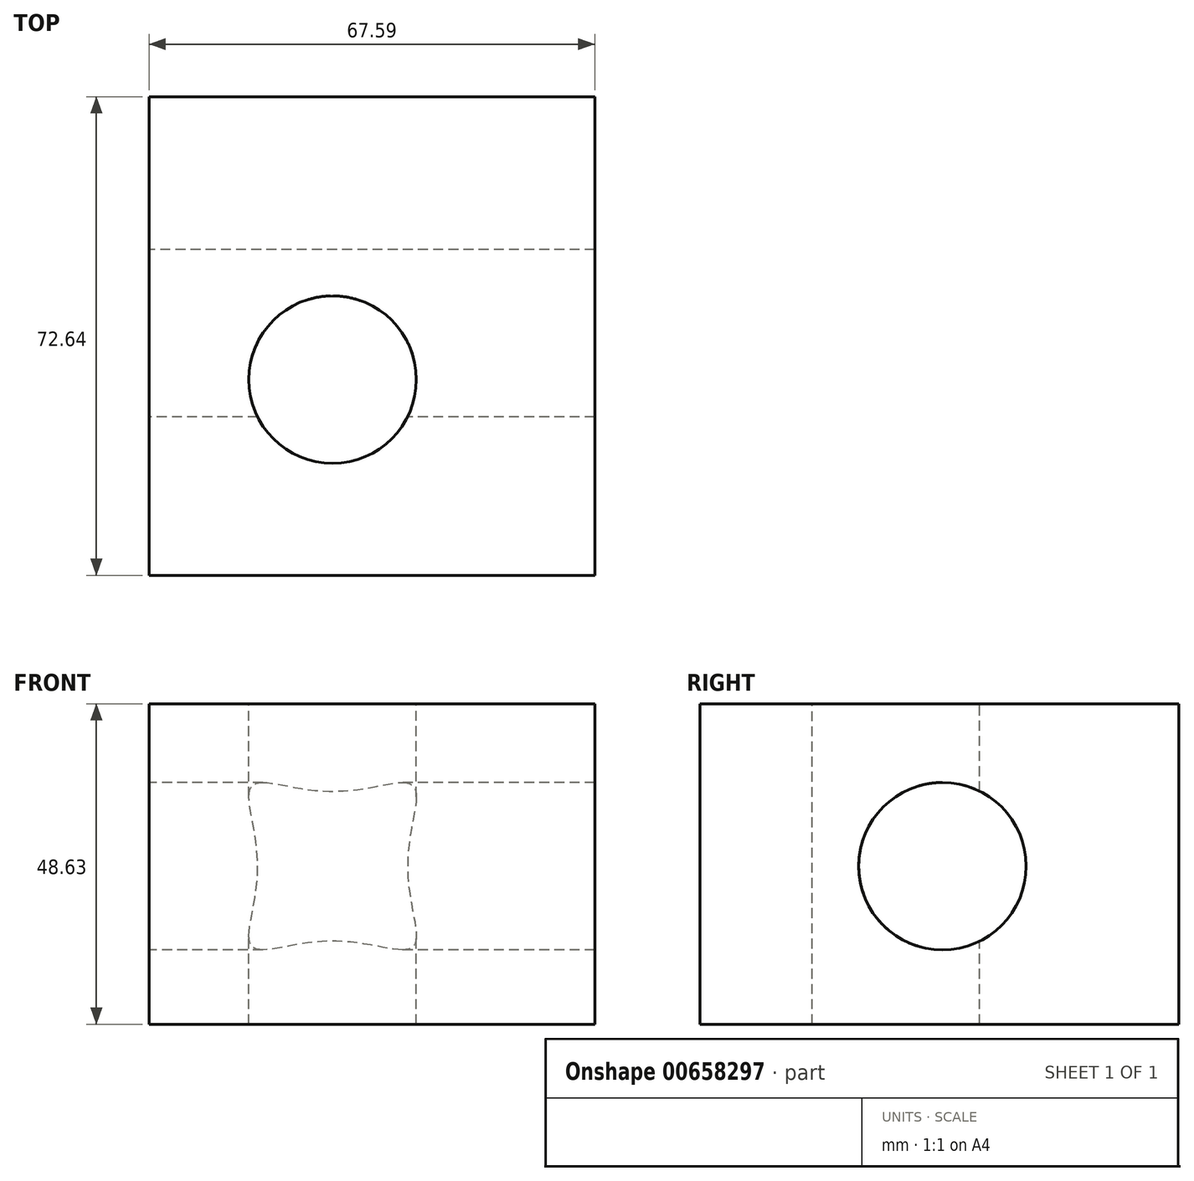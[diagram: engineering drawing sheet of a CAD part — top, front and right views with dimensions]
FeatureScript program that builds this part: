
annotation { "Feature Type Name" : "Feature", "Feature Type Description" : "" }
export const myFeature = defineFeature(function(context is Context, id is Id, definition is map)
    precondition{}
    {
        {
            var Q0;
            Q0=qCreatedBy(makeId("Front.planeOp"),FACE);
            var sketch = newSketch(context, id + "F0", { "sketchPlane" : qUnion([Q0])});
            skLineSegment(sketch, "E0.bottom", {"start": v(0, 0) * mm, "end": v(67.6, 0) * mm});
            skLineSegment(sketch, "E0.top", {"start": v(0, 48.63) * mm, "end": v(67.6, 48.63) * mm});
            skLineSegment(sketch, "E0.left", {"start": v(0, 0) * mm, "end": v(0, 48.63) * mm});
            skLineSegment(sketch, "E0.right", {"start": v(67.6, 0) * mm, "end": v(67.6, 48.63) * mm});
            skSolve(sketch);
        }
        {
            var Q0;
            Q0 = qSketchRegion(id + "F0", true);
            extrude(context, id + "F1", {"entities" : qUnion([Q0]), "depth" : 72.64 * mm, "offsetDistance" : 25.4 * mm});
        }
        {
            var Q0;
            Q0=makeQuery(id+"F1.opExtrude","SWEPT_FACE",FACE,{"disambiguationData":[OSD([sQuery(id+"F0.wireOp",EDGE,"E0.top")])]});
            var sketch = newSketch(context, id + "F2", { "sketchPlane" : qUnion([Q0])});
            skCircle(sketch, "E1", {"center": v(27.83, -42.93) * mm, "radius": 17.12 * mm});
            skSolve(sketch);
        }
        {
            var Q0;
            Q0=sQuery(id+"F2.wireOp",VERTEX,"E1.center");
            var Q1;
            Q1=makeQuery(id+"F1.opExtrude","SWEPT_BODY",BODY,{"disambiguationData":[OSD([sQuery(id+"F0.wireOp",EDGE,"E0.bottom"),sQuery(id+"F0.wireOp",EDGE,"E0.top"),sQuery(id+"F0.wireOp",EDGE,"E0.left"),sQuery(id+"F0.wireOp",EDGE,"E0.right")])]});
            hole(context, id + "F3", {"style" : HoleStyle.SIMPLE, "endStyle" : HoleEndStyle.THROUGH, "holeDiameter" : 25.4 * mm, "majorDiameter" : 6.35 * mm, "isTappedThrough" : true, "tappedDepth" : 12.7 * mm, "tapClearance" : 3, "locations" : qUnion([Q0]), "scope" : qUnion([Q1])});
        }
        {
            var Q0;
            Q0=makeQuery(id+"F1.opExtrude","SWEPT_FACE",FACE,{"disambiguationData":[OSD([sQuery(id+"F0.wireOp",EDGE,"E0.left")])]});
            var sketch = newSketch(context, id + "F4", { "sketchPlane" : qUnion([Q0])});
            skCircle(sketch, "E2", {"center": v(35.88, 23.98) * mm, "radius": 8.76 * mm});
            skSolve(sketch);
        }
        {
            var Q0;
            Q0=sQuery(id+"F4.wireOp",VERTEX,"E2.center");
            var Q1;
            Q1=makeQuery(id+"F1.opExtrude","SWEPT_BODY",BODY,{"disambiguationData":[OSD([sQuery(id+"F0.wireOp",EDGE,"E0.bottom"),sQuery(id+"F0.wireOp",EDGE,"E0.top"),sQuery(id+"F0.wireOp",EDGE,"E0.left"),sQuery(id+"F0.wireOp",EDGE,"E0.right")])]});
            hole(context, id + "F5", {"style" : HoleStyle.SIMPLE, "endStyle" : HoleEndStyle.THROUGH, "holeDiameter" : 25.4 * mm, "majorDiameter" : 6.35 * mm, "isTappedThrough" : true, "tappedDepth" : 12.7 * mm, "tapClearance" : 3, "locations" : qUnion([Q0]), "scope" : qUnion([Q1])});
        }
    });
